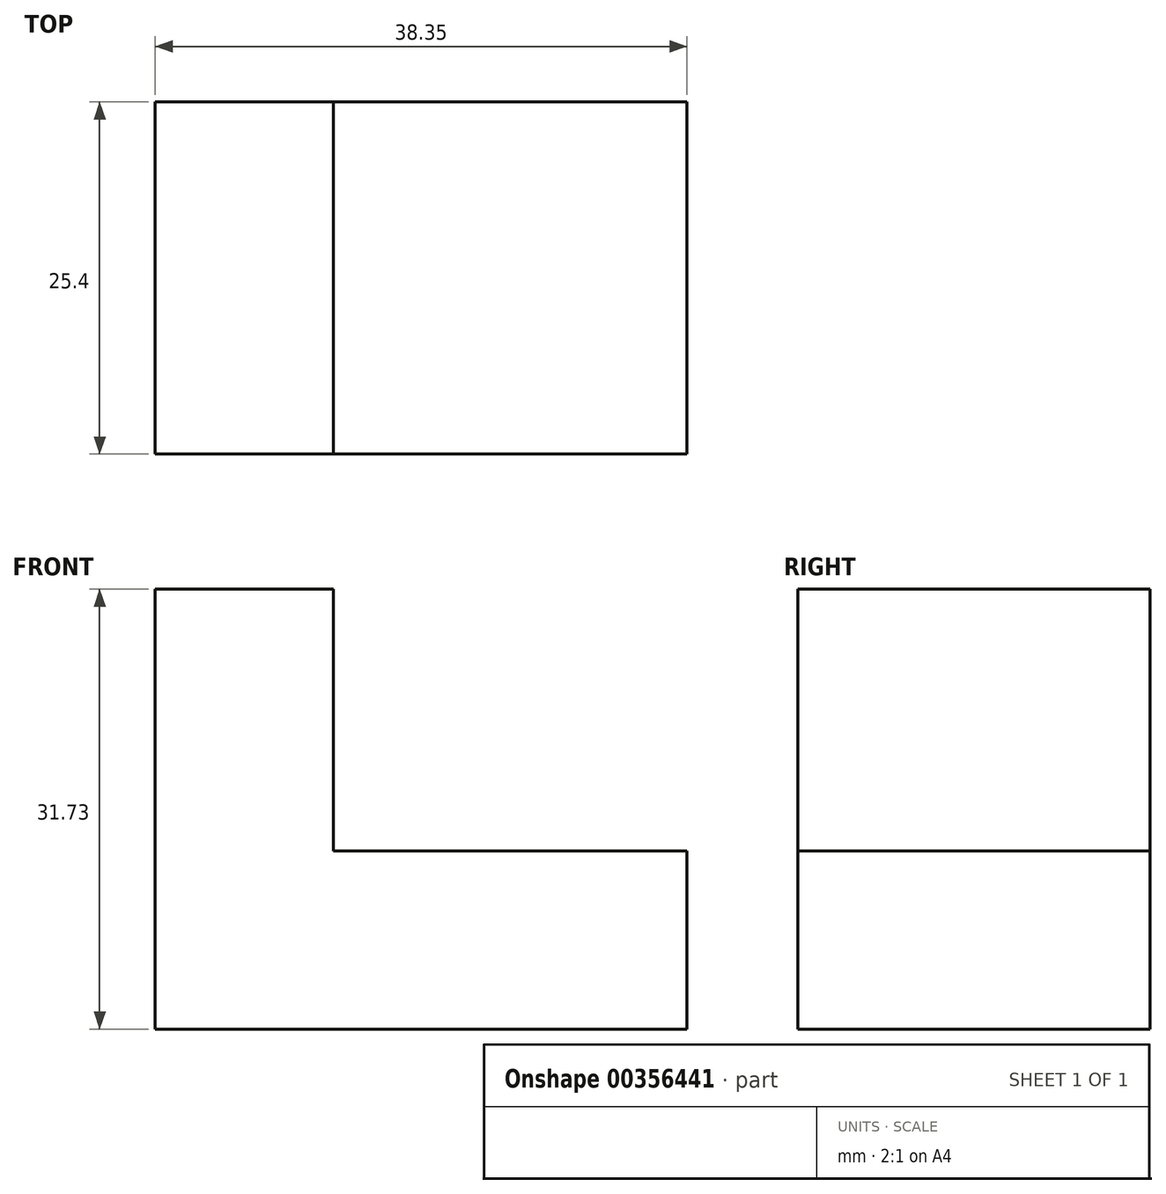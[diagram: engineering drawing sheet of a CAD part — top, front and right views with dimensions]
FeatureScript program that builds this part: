
annotation { "Feature Type Name" : "Feature", "Feature Type Description" : "" }
export const myFeature = defineFeature(function(context is Context, id is Id, definition is map)
    precondition{}
    {
        {
            var Q0;
            Q0=qCreatedBy(makeId("Front.planeOp"),FACE);
            var sketch = newSketch(context, id + "F0", { "sketchPlane" : qUnion([Q0])});
            skLineSegment(sketch, "E0", {"start": v(-30.56, 0) * mm, "end": v(-30.56, 31.73) * mm});
            skLineSegment(sketch, "E1", {"start": v(-30.56, 31.73) * mm, "end": v(-17.72, 31.73) * mm});
            skLineSegment(sketch, "E2", {"start": v(-17.72, 31.73) * mm, "end": v(-17.72, 12.85) * mm});
            skLineSegment(sketch, "E3", {"start": v(-17.72, 12.85) * mm, "end": v(7.79, 12.85) * mm});
            skLineSegment(sketch, "E4", {"start": v(7.79, 12.85) * mm, "end": v(7.79, 0) * mm});
            skLineSegment(sketch, "E5", {"start": v(-30.56, 0) * mm, "end": v(7.79, 0) * mm});
            skSolve(sketch);
        }
        {
            var Q0;
            Q0 = qSketchRegion(id + "F0", true);
            extrude(context, id + "F1", {"entities" : qUnion([Q0]), "depth" : 25.4 * mm});
        }
    });
